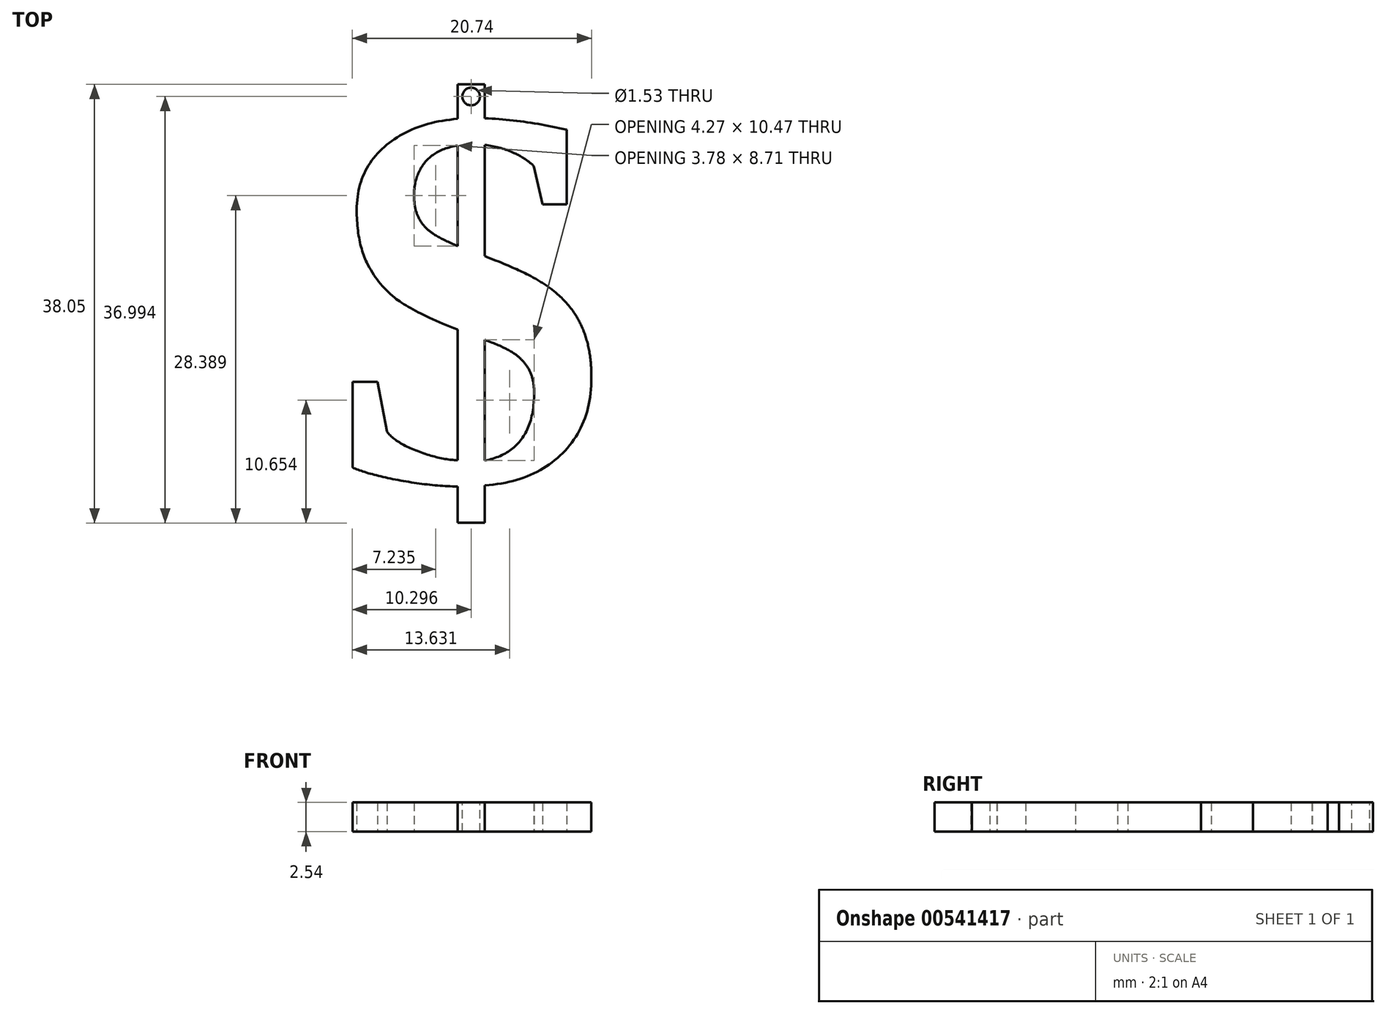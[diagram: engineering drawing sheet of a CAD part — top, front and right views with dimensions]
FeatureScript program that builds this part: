
annotation { "Feature Type Name" : "Feature", "Feature Type Description" : "" }
export const myFeature = defineFeature(function(context is Context, id is Id, definition is map)
    precondition{}
    {
        {
            var Q0;
            Q0=qCreatedBy(makeId("Top.planeOp"),FACE);
            var sketch = newSketch(context, id + "F0", { "sketchPlane" : qUnion([Q0])});
            skText(sketch, "E0", { "text": "$", "fontName": "Tinos-Bold.ttf"});
            skCircle(sketch, "E1", {"center": v(12.06, 33.06) * mm, "radius": 0.64 * mm, "construction": true});
            const initialGuessF0  = {"E0": [0, 0, 1, 0, 0.03423]};
            skSetInitialGuess(sketch, initialGuessF0);
            skSolve(sketch);
        }
        {
            var Q0;
            Q0=makeQuery(id+"F0.imprint","IMPRINT",FACE,{"disambiguationData":[TD([[makeQuery(id+"F0.imprint","IMPRINT",EDGE,{"derivedFrom":sQuery(id+"F0.wireOp",EDGE,"E0.sketch_text.stroke-0")}),-1.0]])]});
            extrude(context, id + "F1", {"entities" : qUnion([Q0]), "depth" : 2.54 * mm, "offsetDistance" : 25.4 * mm});
        }
        {
            var Q0;
            Q0=makeQuery(id+"F1.opExtrude","CAP_FACE",FACE,{"disambiguationData":[OSD([sQuery(id+"F0.wireOp",EDGE,"E0.sketch_text.stroke-0"),sQuery(id+"F0.wireOp",EDGE,"E0.sketch_text.stroke-1"),sQuery(id+"F0.wireOp",EDGE,"E0.sketch_text.stroke-2"),sQuery(id+"F0.wireOp",EDGE,"E0.sketch_text.stroke-3"),sQuery(id+"F0.wireOp",EDGE,"E0.sketch_text.stroke-4"),sQuery(id+"F0.wireOp",EDGE,"E0.sketch_text.stroke-5"),sQuery(id+"F0.wireOp",EDGE,"E0.sketch_text.stroke-6"),sQuery(id+"F0.wireOp",EDGE,"E0.sketch_text.stroke-7"),sQuery(id+"F0.wireOp",EDGE,"E0.sketch_text.stroke-8"),sQuery(id+"F0.wireOp",EDGE,"E0.sketch_text.stroke-9"),sQuery(id+"F0.wireOp",EDGE,"E0.sketch_text.stroke-10"),sQuery(id+"F0.wireOp",EDGE,"E0.sketch_text.stroke-11"),sQuery(id+"F0.wireOp",EDGE,"E0.sketch_text.stroke-12"),sQuery(id+"F0.wireOp",EDGE,"E0.sketch_text.stroke-13"),sQuery(id+"F0.wireOp",EDGE,"E0.sketch_text.stroke-14"),sQuery(id+"F0.wireOp",EDGE,"E0.sketch_text.stroke-15"),sQuery(id+"F0.wireOp",EDGE,"E0.sketch_text.stroke-16"),sQuery(id+"F0.wireOp",EDGE,"E0.sketch_text.stroke-17"),sQuery(id+"F0.wireOp",EDGE,"E0.sketch_text.stroke-18"),sQuery(id+"F0.wireOp",EDGE,"E0.sketch_text.stroke-19"),sQuery(id+"F0.wireOp",EDGE,"E0.sketch_text.stroke-20"),sQuery(id+"F0.wireOp",EDGE,"E0.sketch_text.stroke-21"),sQuery(id+"F0.wireOp",EDGE,"E0.sketch_text.stroke-22"),sQuery(id+"F0.wireOp",EDGE,"E0.sketch_text.stroke-23"),sQuery(id+"F0.wireOp",EDGE,"E0.sketch_text.stroke-24"),sQuery(id+"F0.wireOp",EDGE,"E0.sketch_text.stroke-25"),sQuery(id+"F0.wireOp",EDGE,"E0.sketch_text.stroke-26"),sQuery(id+"F0.wireOp",EDGE,"E0.sketch_text.stroke-27"),sQuery(id+"F0.wireOp",EDGE,"E0.sketch_text.stroke-28"),sQuery(id+"F0.wireOp",EDGE,"E0.sketch_text.stroke-29"),sQuery(id+"F0.wireOp",EDGE,"E0.sketch_text.stroke-30"),sQuery(id+"F0.wireOp",EDGE,"E0.sketch_text.stroke-31"),sQuery(id+"F0.wireOp",EDGE,"E0.sketch_text.stroke-32"),sQuery(id+"F0.wireOp",EDGE,"E0.sketch_text.stroke-33"),sQuery(id+"F0.wireOp",EDGE,"E0.sketch_text.stroke-34"),sQuery(id+"F0.wireOp",EDGE,"E0.sketch_text.stroke-35"),sQuery(id+"F0.wireOp",EDGE,"E0.sketch_text.stroke-36"),sQuery(id+"F0.wireOp",EDGE,"E0.sketch_text.stroke-37"),sQuery(id+"F0.wireOp",EDGE,"E0.sketch_text.stroke-38"),sQuery(id+"F0.wireOp",EDGE,"E0.sketch_text.stroke-39"),sQuery(id+"F0.wireOp",EDGE,"E0.sketch_text.stroke-40"),sQuery(id+"F0.wireOp",EDGE,"E0.sketch_text.stroke-41"),sQuery(id+"F0.wireOp",EDGE,"E0.sketch_text.stroke-42"),sQuery(id+"F0.wireOp",EDGE,"E0.sketch_text.stroke-43"),sQuery(id+"F0.wireOp",EDGE,"E0.sketch_text.stroke-44")])],"isStart":false});
            var sketch = newSketch(context, id + "F2", { "sketchPlane" : qUnion([Q0])});
            skCircle(sketch, "E2", {"center": v(11.99, 33.36) * mm, "radius": 0.76 * mm});
            skSolve(sketch);
        }
        {
            var Q0;
            Q0 = qSketchRegion(id + "F2", true);
            extrude(context, id + "F3", {"entities" : qUnion([Q0]), "operationType" : NewBodyOperationType.REMOVE, "oppositeDirection" : true, "depth" : 25.4 * mm, "offsetDistance" : 25.4 * mm});
        }
    });
